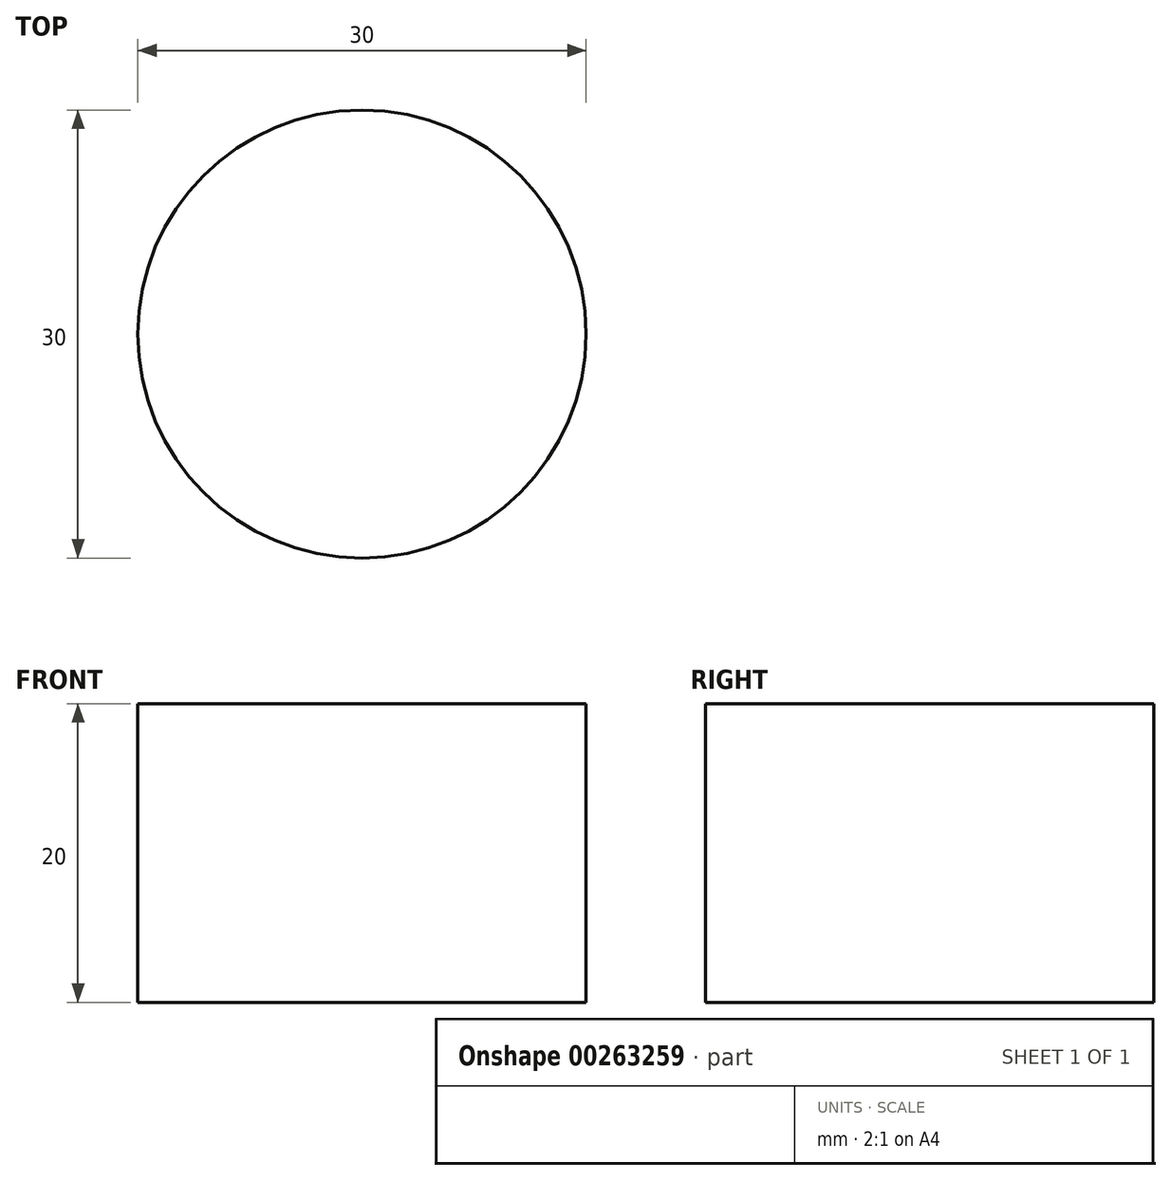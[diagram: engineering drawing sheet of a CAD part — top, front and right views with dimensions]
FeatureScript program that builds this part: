
annotation { "Feature Type Name" : "Feature", "Feature Type Description" : "" }
export const myFeature = defineFeature(function(context is Context, id is Id, definition is map)
    precondition{}
    {
        {
            var Q0;
            Q0=qCreatedBy(makeId("Top.planeOp"),FACE);
            var sketch = newSketch(context, id + "F0", { "sketchPlane" : qUnion([Q0])});
            skCircle(sketch, "E0", {"center": v(0, 0) * mm, "radius": 15 * mm});
            skSolve(sketch);
        }
        {
            var Q0;
            Q0 = qSketchRegion(id + "F0", true);
            extrude(context, id + "F1", {"entities" : qUnion([Q0]), "depth" : 20 * mm});
        }
    });
